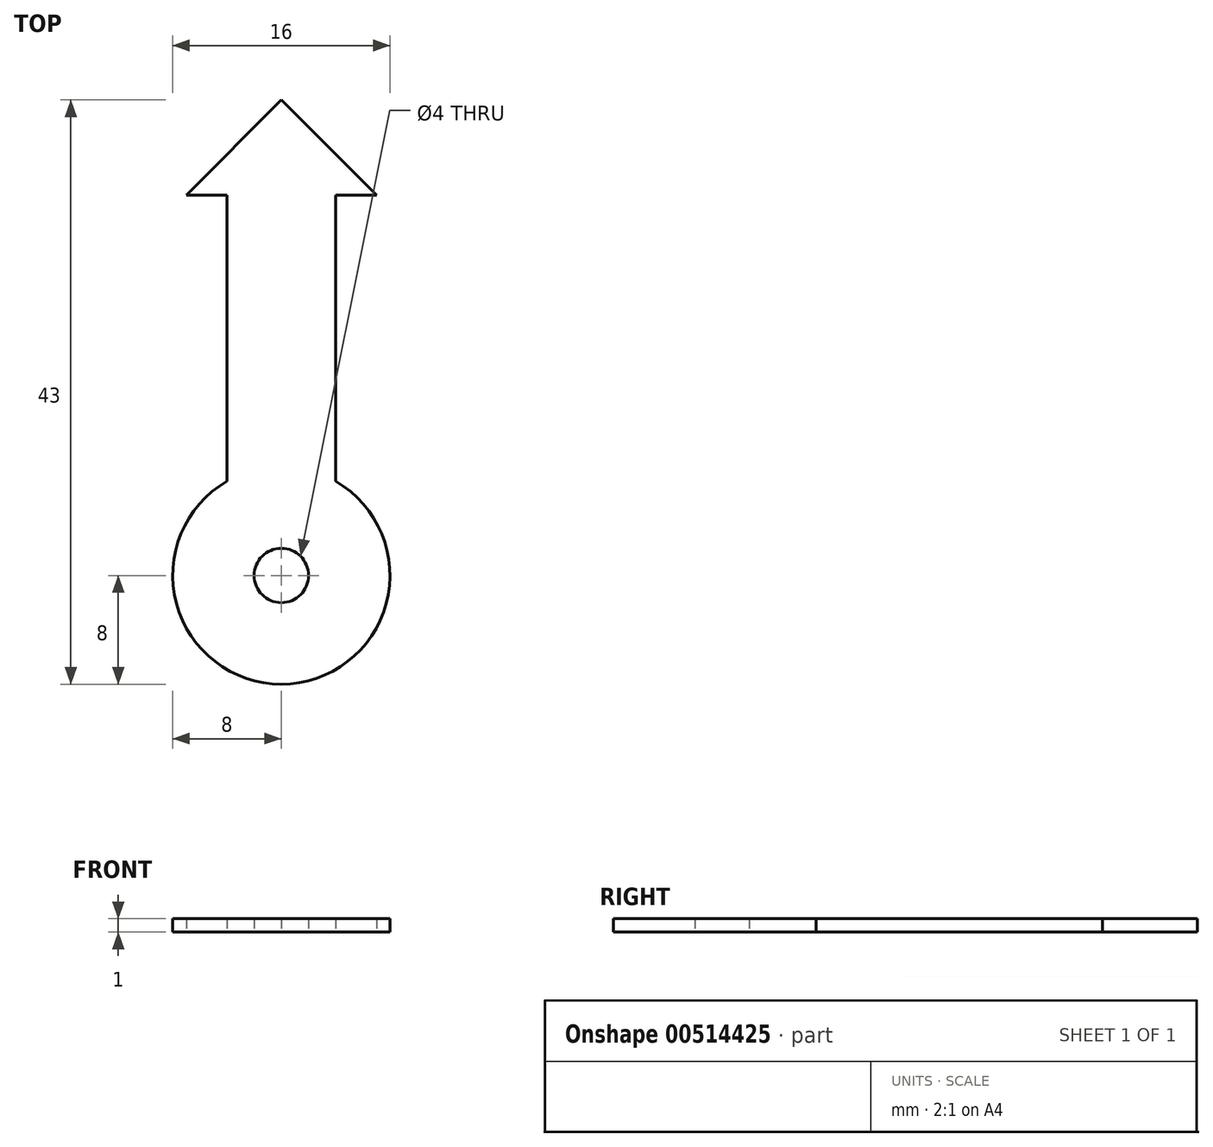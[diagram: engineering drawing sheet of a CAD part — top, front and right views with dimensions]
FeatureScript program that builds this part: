
annotation { "Feature Type Name" : "Feature", "Feature Type Description" : "" }
export const myFeature = defineFeature(function(context is Context, id is Id, definition is map)
    precondition{}
    {
        {
            var Q0;
            Q0=qCreatedBy(makeId("Top.planeOp"),FACE);
            var sketch = newSketch(context, id + "F0", { "sketchPlane" : qUnion([Q0])});
            skCircle(sketch, "E0", {"center": v(0, 0) * mm, "radius": 2 * mm});
            skCircle(sketch, "E1", {"center": v(0, 0) * mm, "radius": 8 * mm});
            skLineSegment(sketch, "E2", {"start": v(0, 0) * mm, "end": v(0, 35) * mm});
            skLineSegment(sketch, "E3", {"start": v(0, 35) * mm, "end": v(-7, 28) * mm});
            skLineSegment(sketch, "E4", {"start": v(-7, 28) * mm, "end": v(-4, 28) * mm});
            skLineSegment(sketch, "E5", {"start": v(-4, 28) * mm, "end": v(-4, 6.93) * mm});
            skLineSegment(sketch, "E6.MirrorCS", {"start": v(0, 35) * mm, "end": v(7, 28) * mm});
            skLineSegment(sketch, "E7.MirrorCS", {"start": v(7, 28) * mm, "end": v(4, 28) * mm});
            skLineSegment(sketch, "E8.MirrorCS", {"start": v(4, 28) * mm, "end": v(4, 6.93) * mm});
            skSolve(sketch);
        }
        {
            var Q0;
            {var subQ0=sQuery(id+"F0.wireOp",EDGE,"E3");Q0=makeQuery(id+"F0.imprint","IMPRINT",FACE,{"disambiguationData":[TD([[makeQuery(id+"F0.imprint","IMPRINT",EDGE,{"derivedFrom":subQ0}),1.0]])]});}
            var Q1;
            {var subQ0=sQuery(id+"F0.wireOp",EDGE,"E6.MirrorCS");Q1=makeQuery(id+"F0.imprint","IMPRINT",FACE,{"disambiguationData":[TD([[makeQuery(id+"F0.imprint","IMPRINT",EDGE,{"derivedFrom":subQ0}),-1.0]])]});}
            var Q2;
            Q2=makeQuery(id+"F0.imprint","IMPRINT",FACE,{"disambiguationData":[TD([[makeQuery(id+"F0.imprint","IMPRINT",EDGE,{"derivedFrom":sQuery(id+"F0.wireOp",EDGE,"E0")}),-1.0]])]});
            extrude(context, id + "F1", {"entities" : qUnion([Q0, Q1, Q2]), "depth" : 1 * mm});
        }
    });
